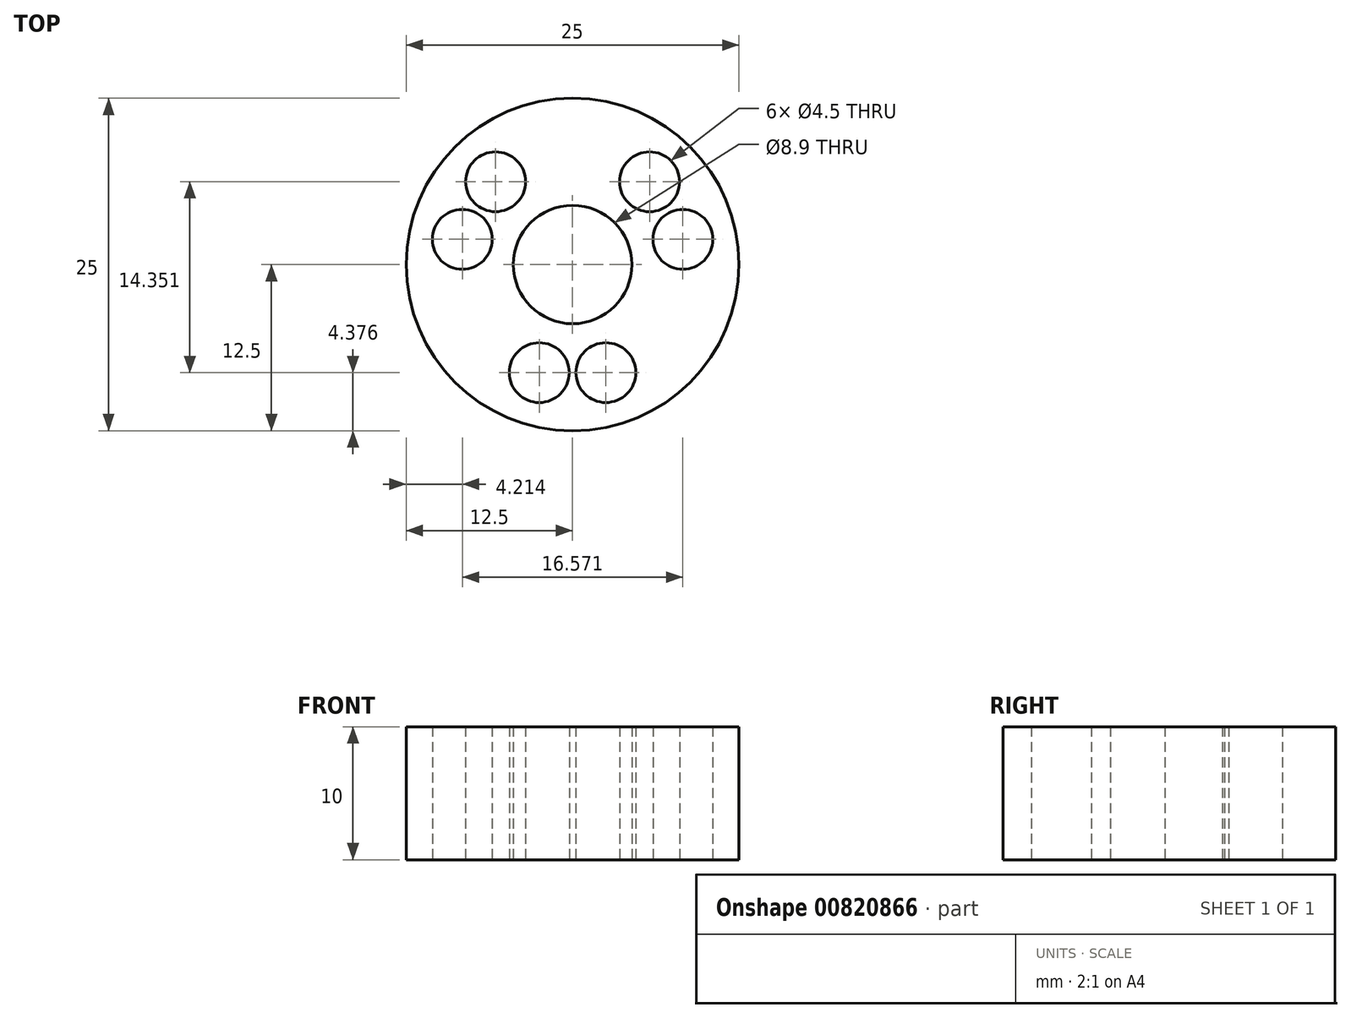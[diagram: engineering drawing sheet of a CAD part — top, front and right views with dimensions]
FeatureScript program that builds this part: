
annotation { "Feature Type Name" : "Feature", "Feature Type Description" : "" }
export const myFeature = defineFeature(function(context is Context, id is Id, definition is map)
    precondition{}
    {
        {
            var Q0;
            Q0=qCreatedBy(makeId("Top.planeOp"),FACE);
            var sketch = newSketch(context, id + "F0", { "sketchPlane" : qUnion([Q0])});
            skCircle(sketch, "E0", {"center": v(0, 0) * mm, "radius": 12.5 * mm});
            skCircle(sketch, "E1", {"center": v(0, 0) * mm, "radius": 8.5 * mm, "construction": true});
            skCircle(sketch, "E2", {"center": v(-2.5, -8.12) * mm, "radius": 2.25 * mm});
            skCircle(sketch, "E3", {"center": v(2.5, -8.12) * mm, "radius": 2.25 * mm});
            skCircle(sketch, "E4", {"center": v(8.29, 1.9) * mm, "radius": 2.25 * mm});
            skCircle(sketch, "E5", {"center": v(5.79, 6.23) * mm, "radius": 2.25 * mm});
            skCircle(sketch, "E6", {"center": v(-5.79, 6.23) * mm, "radius": 2.25 * mm});
            skCircle(sketch, "E7", {"center": v(-8.29, 1.9) * mm, "radius": 2.25 * mm});
            skLineSegment(sketch, "E8", {"start": v(0, 0) * mm, "end": v(7.36, 4.25) * mm, "construction": true});
            skLineSegment(sketch, "E9", {"start": v(0, 0) * mm, "end": v(-7.36, 4.25) * mm, "construction": true});
            skLineSegment(sketch, "E10", {"start": v(0, 0) * mm, "end": v(0, -8.5) * mm, "construction": true});
            skCircle(sketch, "E11", {"center": v(0, 0) * mm, "radius": 4.45 * mm});
            skSolve(sketch);
        }
        {
            var Q0;
            Q0=makeQuery(id+"F0.imprint","IMPRINT",FACE,{"disambiguationData":[TD([[makeQuery(id+"F0.imprint","IMPRINT",EDGE,{"derivedFrom":sQuery(id+"F0.wireOp",EDGE,"E0")}),1.0]])]});
            extrude(context, id + "F1", {"entities" : qUnion([Q0]), "depth" : 10 * mm, "offsetDistance" : 25 * mm});
        }
    });
